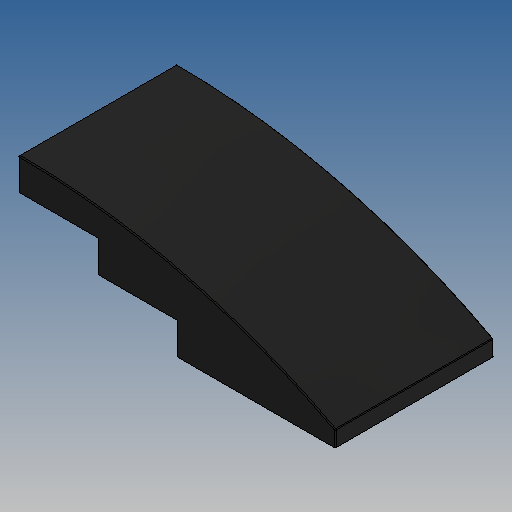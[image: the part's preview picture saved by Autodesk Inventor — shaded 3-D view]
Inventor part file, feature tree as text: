
AUTODESK INVENTOR PART (.ipt)
format: ipt  version: 2025 (Build 290162010, 162A)  size: 260,608 bytes
history: native  units: in
note: dims shown in document units (in); Inventor stores cm internally (conversion verified against a paired STEP export)
features: extrude x6, other x6, sketch x5, fillet x1
ambient origin geometry x8: Origin, YZ Plane, XZ Plane, XY Plane, X Axis, Y Axis, Z Axis, Center Point
bodies: Solid1 (feature_tree)
feature tree (18):
  extrude  "Extrusion1"  Depth=0.6299in
  sketch  "Sketch10"  dims[d22=0.0039in d89=0.0in d90=0.0in]
  extrude  "Extrusion7"  Depth=0.378in TaperAngle=0.0deg
  extrude  "Extrusion8"  TaperAngle=0.0deg  [1 undecoded]
  extrude  "Extrusion2"  Depth=0.189in
  extrude  "Extrusion9"  Depth=0.063in
  extrude  "Extrusion10"  Depth=0.063in
  fillet  "Fillet1"  Radius=0.063in
  other  "Work Axis2"
  other  "Work Axis3"
  other  "Work Axis4"
  other  "Work Axis5"
  other  "Work Axis6"
  other  "Work Axis7"
  sketch  "Sketch2"  dims[d0=1.2598in d1=0.6299in]
  sketch  "Sketch3"  dims[d4=0.378in d5=0.0in d7=0.0591in d11=0.3307in d12=0.0in]
  sketch  "Sketch11"  dims[d95=0.315in d96=0.0in d97=0.189in]
  sketch  "Sketch12"  dims[d98=0.0in d100=0.063in d102=0.063in d103=0.063in d104=0.063in d105=0.063in d107=0.063in d108=0.063in d109=0.5039in d110=0.0in d112=0.0in d113=0.252in d114=0.126in d115=0.6299in d116=0.063in d119=0.0472in d120=0.3937in d121=0.0in d122=0.0472in d123=0.3937in d124=0.0in d125=0.0in d126=0.0in d127=0.0in d128=0.0in d129=0.189in d130=0.189in d132=0.0in d133=0.0in d134=0.0in d135=0.0in d136=0.0in]
note: 1 required parameter value undecoded (feature->parameter linkage not recoverable at this tier; creation-order binding heuristic only, values carry confidence <= 0.55)
